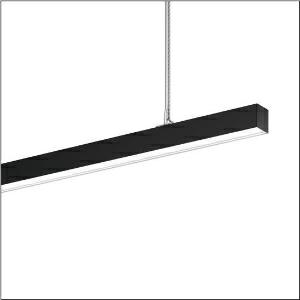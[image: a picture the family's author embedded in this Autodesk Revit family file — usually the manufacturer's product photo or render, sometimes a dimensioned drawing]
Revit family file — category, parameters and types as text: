
# Revit family: silica_r__21_51mx33dc3dbb_6d07
name_source: partatom
category: Lighting Fixtures
units: mm (PartAtom-declared; Revit-internal decimal feet)

## family parameters
Cut with Voids When Loaded = No
Host = Face
Light Source = No
Part Type = Normal
Room Calculation Point = No
Round Connector Dimension = Use Diameter
Shared = No

## types (1)
- --- (1 x LED, 14780 lm, 99.5 W, 3000K)
    Apparent Load = 100 VA
    CIE Flux Codes = 78 96 99 55 100
    Color Rendering = 80
    Color Temperature = 3000K
    Default Elevation = 1800 mm
    Description = Silica® 21, office luminaire, primary optical cover: prismatic diffuser, of PMMA, CAT 2 (L<= 3000cd/m²), light emission: direct/indirect distribution, primary light characteristic: symmetric, installation type: suspended mounting, LED, rated luminous flux: 14.780lm, luminous efficacy: 149lm/W, light colour: 830, colour temperature: 3000K, with terminal, 3+2-pole, max. 2.5mm², mains connection: 220..240V, AC, 50/60Hz, rated input power: 99.5W, luminaire housing, of aluminium, jet black (RAL 9005), length: 3.004mm, width: 53mm, height: 53mm, protection rating (complete): IP20, insulation class (complete): insulation class I (protective earthing), certification: CE, permissible operating ambient temperature: 0..+35°C, standard: EN 50419, packaging unit: 1 piece
    Height = 53 mm
    Lamp = 1 x LED
    Lamp Light Flux = 14780 lm
    Lamp Power = 99.5 W
    Lamp count = 1
    Length = 3004 mm
    Luminous efficacy = 149 lm/W
    Manufacturer = Siteco
    ModVariant = No
    Model = 51MX33DC3DBB
    Mounting Place = Ceiling
    Mounting Type = Pendant
    Number of Poles = 1
    OnlyDefault = Yes
    Power Factor = 1
    Product Name = Silica® 21
    Product group = office luminaire | ceiling pendant
    ProductGroupID = 902
    Protection Class = Protection class I
    Protection Degree = IP 20
    RLX_Detail_Level = 1
    RLX_Emergency_Light_Flux = 0 lm
    RLX_Emergency_Type = 0
    RLX_Emergency_Type_DB = No
    RlxData = <blob elided: 26093 chars, md5=da6ea5c0>
    Socket = socket
    Standby Power = 0 W
    System Light Flux = 14780 lm
    System Power = 100 W
    Type Comments = factory setting: luminous flux: 100 % | dim-lin: 254 | 345 mA
    Type Image = l_1313646.jpg
    URL = http://relux.com
    VarID = @adj_067145
    Voltage = 0 V
    Weight = 0.00 kg
    Width = 53 mm

## geometry (parser evidence)
native form markers: Blend x4, Sweep x13
no freeform markers — native parametric forms only
